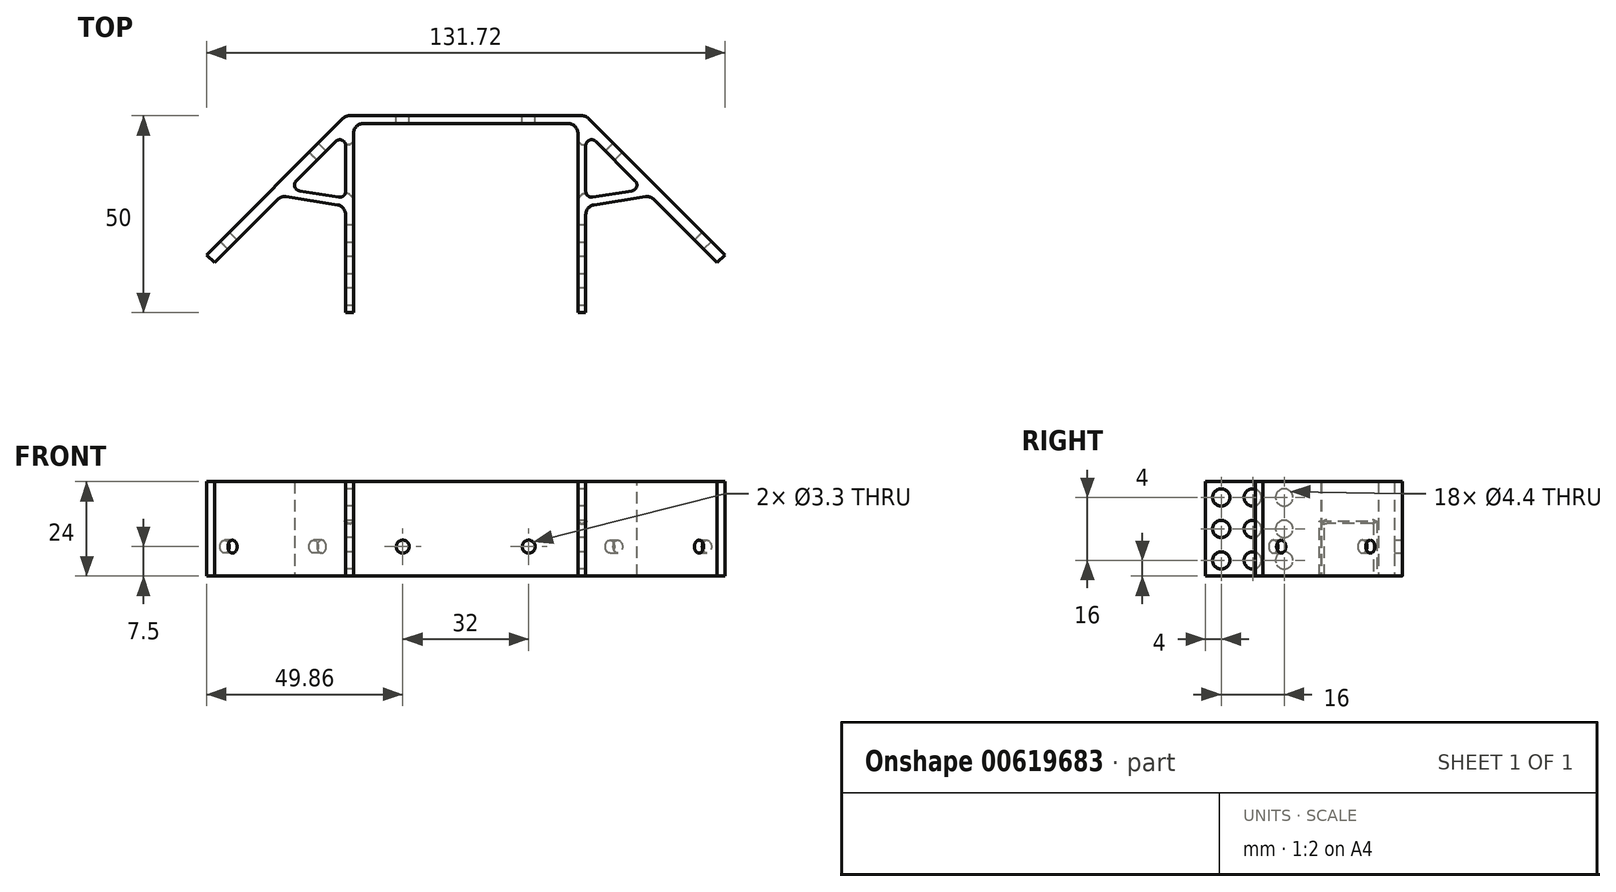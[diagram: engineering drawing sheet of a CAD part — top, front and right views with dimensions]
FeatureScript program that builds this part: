
annotation { "Feature Type Name" : "Feature", "Feature Type Description" : "" }
export const myFeature = defineFeature(function(context is Context, id is Id, definition is map)
    precondition{}
    {
        {
            var Q0;
            Q0=qCreatedBy(makeId("Top.planeOp"),FACE);
            var sketch = newSketch(context, id + "F0", { "sketchPlane" : qUnion([Q0])});
            skLineSegment(sketch, "E0.bottom", {"start": v(-28.5, 16) * mm, "end": v(28.5, 16) * mm});
            skLineSegment(sketch, "E0.left", {"start": v(-28.5, 16) * mm, "end": v(-28.5, -32) * mm});
            skLineSegment(sketch, "E0.right", {"start": v(28.5, 16) * mm, "end": v(28.5, -32) * mm});
            skLineSegment(sketch, "E1.bottom", {"start": v(-30.5, 18) * mm, "end": v(30.5, 18) * mm});
            skLineSegment(sketch, "E1.top", {"start": v(-30.5, -32) * mm, "end": v(-28.5, -32) * mm});
            skLineSegment(sketch, "E1.left", {"start": v(-30.5, 14) * mm, "end": v(-30.5, -2.97) * mm});
            skLineSegment(sketch, "E1.right", {"start": v(30.5, 14) * mm, "end": v(30.5, -2.97) * mm});
            skLineSegment(sketch, "E2", {"start": v(-30.5, 18) * mm, "end": v(-65.86, -17.36) * mm});
            skLineSegment(sketch, "E3", {"start": v(-30.5, 14) * mm, "end": v(-45.14, -0.64) * mm});
            skLineSegment(sketch, "E4", {"start": v(30.5, 18) * mm, "end": v(65.86, -17.36) * mm});
            skLineSegment(sketch, "E5", {"start": v(30.5, 14) * mm, "end": v(45.14, -0.64) * mm});
            skLineSegment(sketch, "E6", {"start": v(-65.86, -17.36) * mm, "end": v(-63.86, -19.36) * mm});
            skLineSegment(sketch, "E7", {"start": v(65.86, -17.36) * mm, "end": v(63.86, -19.36) * mm});
            skLineSegment(sketch, "E8.trimOffspring", {"start": v(28.5, -32) * mm, "end": v(30.5, -32) * mm});
            skLineSegment(sketch, "E9", {"start": v(-46.88, -2.38) * mm, "end": v(-30.5, -5) * mm});
            skLineSegment(sketch, "E10", {"start": v(-30.5, -2.97) * mm, "end": v(-45.14, -0.64) * mm});
            skLineSegment(sketch, "E11", {"start": v(30.5, -5) * mm, "end": v(46.88, -2.38) * mm});
            skLineSegment(sketch, "E12", {"start": v(45.14, -0.64) * mm, "end": v(30.5, -2.97) * mm});
            skLineSegment(sketch, "E13.trimOffspring", {"start": v(-46.88, -2.38) * mm, "end": v(-63.86, -19.36) * mm});
            skLineSegment(sketch, "E14.trimOffspring", {"start": v(-30.5, -5) * mm, "end": v(-30.5, -32) * mm});
            skLineSegment(sketch, "E15.trimOffspring", {"start": v(30.5, -5) * mm, "end": v(30.5, -32) * mm});
            skLineSegment(sketch, "E16.trimOffspring", {"start": v(46.88, -2.38) * mm, "end": v(63.86, -19.36) * mm});
            skSolve(sketch);
        }
        {
            var Q0;
            Q0=makeQuery(id+"F0.imprint","IMPRINT",FACE,{"disambiguationData":[TD([[makeQuery(id+"F0.imprint","IMPRINT",EDGE,{"derivedFrom":sQuery(id+"F0.wireOp",EDGE,"E0.bottom")}),1.0]])]});
            extrude(context, id + "F1", {"entities" : qUnion([Q0]), "depth" : 24 * mm, "offsetDistance" : 25 * mm});
        }
        {
            var Q0;
            Q0=makeQuery(id+"F1.opExtrude","SWEPT_FACE",FACE,{"disambiguationData":[OSD([sQuery(id+"F0.wireOp",EDGE,"E4")])]});
            var sketch = newSketch(context, id + "F2", { "sketchPlane" : qUnion([Q0])});
            skPoint(sketch, "E17", {"position": v(-20.34, 7.5) * mm});
            skPoint(sketch, "E18", {"position": v(-52.34, 7.5) * mm});
            skSolve(sketch);
        }
        {
            var Q0;
            Q0=sQuery(id+"F2.wireOp",VERTEX,"E17");
            var Q1;
            Q1=sQuery(id+"F2.wireOp",VERTEX,"E18");
            var Q2;
            Q2=makeQuery(id+"F1.opExtrude","SWEPT_BODY",BODY,{"disambiguationData":[OSD([sQuery(id+"F0.wireOp",EDGE,"E0.bottom"),sQuery(id+"F0.wireOp",EDGE,"E0.left"),sQuery(id+"F0.wireOp",EDGE,"E0.right"),sQuery(id+"F0.wireOp",EDGE,"E1.bottom"),sQuery(id+"F0.wireOp",EDGE,"E1.top"),sQuery(id+"F0.wireOp",EDGE,"E1.left"),sQuery(id+"F0.wireOp",EDGE,"E1.right"),sQuery(id+"F0.wireOp",EDGE,"E2"),sQuery(id+"F0.wireOp",EDGE,"E3"),sQuery(id+"F0.wireOp",EDGE,"E4"),sQuery(id+"F0.wireOp",EDGE,"E5"),sQuery(id+"F0.wireOp",EDGE,"E6"),sQuery(id+"F0.wireOp",EDGE,"E7"),sQuery(id+"F0.wireOp",EDGE,"E8.trimOffspring")])]});
            hole(context, id + "F3", {"style" : HoleStyle.SIMPLE, "endStyle" : HoleEndStyle.BLIND, "standardTappedOrClearance" : lookupTablePath({ "standard" : "ISO", "fit" : "Normal", "size" : "M3", "type" : "Clearance" }), "standardBlindInLast" : lookupTablePath({ "fit" : "Standard", "standard" : "ISO", "size" : "M3", "type" : "Clearance" }), "holeDiameter" : 3.3 * mm, "majorDiameter" : 3 * mm, "holeDepth" : 3 * mm, "isTappedThrough" : true, "tappedDepth" : 12 * mm, "tapClearance" : 3, "locations" : qUnion([Q0, Q1]), "scope" : qUnion([Q2])});
        }
        {
            var Q0;
            Q0=makeQuery(id+"F1.opExtrude","SWEPT_EDGE",EDGE,{"disambiguationData":[OSD([sQuery(id+"F0.wireOp",EDGE,"E1.left"),sQuery(id+"F0.wireOp",EDGE,"E3")])]});
            var Q1;
            Q1=makeQuery(id+"F1.opExtrude","SWEPT_EDGE",EDGE,{"disambiguationData":[OSD([sQuery(id+"F0.wireOp",EDGE,"E1.right"),sQuery(id+"F0.wireOp",EDGE,"E5")])]});
            var Q2;
            Q2=makeQuery(id+"F1.opExtrude","SWEPT_EDGE",EDGE,{"disambiguationData":[OSD([sQuery(id+"F0.wireOp",EDGE,"E3"),sQuery(id+"F0.wireOp",EDGE,"E10")])]});
            var Q3;
            Q3=makeQuery(id+"F1.opExtrude","SWEPT_EDGE",EDGE,{"disambiguationData":[OSD([sQuery(id+"F0.wireOp",EDGE,"E1.left"),sQuery(id+"F0.wireOp",EDGE,"E10")])]});
            var Q4;
            Q4=makeQuery(id+"F1.opExtrude","SWEPT_EDGE",EDGE,{"disambiguationData":[OSD([sQuery(id+"F0.wireOp",EDGE,"E1.right"),sQuery(id+"F0.wireOp",EDGE,"E12")])]});
            var Q5;
            Q5=makeQuery(id+"F1.opExtrude","SWEPT_EDGE",EDGE,{"disambiguationData":[OSD([sQuery(id+"F0.wireOp",EDGE,"E5"),sQuery(id+"F0.wireOp",EDGE,"E12")])]});
            fillet(context, id + "F4", {"entities" : qUnion([Q0, Q1, Q2, Q3, Q4, Q5]), "radius" : 1.5 * mm, "tangentPropagation" : true, "allowEdgeOverflow" : false});
        }
        {
            var Q0;
            Q0=makeQuery(id+"F1.opExtrude","SWEPT_FACE",FACE,{"disambiguationData":[OSD([sQuery(id+"F0.wireOp",EDGE,"E2")])]});
            var sketch = newSketch(context, id + "F5", { "sketchPlane" : qUnion([Q0])});
            skPoint(sketch, "E19", {"position": v(20.34, 7.5) * mm});
            skPoint(sketch, "E20", {"position": v(52.34, 7.5) * mm});
            skSolve(sketch);
        }
        {
            var Q0;
            Q0=sQuery(id+"F5.wireOp",VERTEX,"E19");
            var Q1;
            Q1=sQuery(id+"F5.wireOp",VERTEX,"E20");
            var Q2;
            Q2=makeQuery(id+"F1.opExtrude","SWEPT_BODY",BODY,{"disambiguationData":[OSD([sQuery(id+"F0.wireOp",EDGE,"E0.bottom"),sQuery(id+"F0.wireOp",EDGE,"E0.left"),sQuery(id+"F0.wireOp",EDGE,"E0.right"),sQuery(id+"F0.wireOp",EDGE,"E1.bottom"),sQuery(id+"F0.wireOp",EDGE,"E1.top"),sQuery(id+"F0.wireOp",EDGE,"E1.left"),sQuery(id+"F0.wireOp",EDGE,"E1.right"),sQuery(id+"F0.wireOp",EDGE,"E2"),sQuery(id+"F0.wireOp",EDGE,"E3"),sQuery(id+"F0.wireOp",EDGE,"E4"),sQuery(id+"F0.wireOp",EDGE,"E5"),sQuery(id+"F0.wireOp",EDGE,"E6"),sQuery(id+"F0.wireOp",EDGE,"E7"),sQuery(id+"F0.wireOp",EDGE,"E8.trimOffspring")])]});
            hole(context, id + "F6", {"style" : HoleStyle.SIMPLE, "endStyle" : HoleEndStyle.BLIND, "standardTappedOrClearance" : lookupTablePath({ "standard" : "ISO", "fit" : "Normal", "size" : "M3", "type" : "Clearance" }), "standardBlindInLast" : lookupTablePath({ "fit" : "Standard", "standard" : "ISO", "size" : "M3", "type" : "Clearance" }), "holeDiameter" : 3.3 * mm, "majorDiameter" : 5 * mm, "holeDepth" : 3 * mm, "isTappedThrough" : true, "tappedDepth" : 12 * mm, "tapClearance" : 3, "locations" : qUnion([Q0, Q1]), "scope" : qUnion([Q2])});
        }
        {
            var Q0;
            Q0=makeQuery(id+"F1.opExtrude","SWEPT_FACE",FACE,{"disambiguationData":[OSD([sQuery(id+"F0.wireOp",EDGE,"E1.bottom")])]});
            var sketch = newSketch(context, id + "F7", { "sketchPlane" : qUnion([Q0])});
            skPoint(sketch, "E21", {"position": v(-16, 7.5) * mm});
            skPoint(sketch, "E22", {"position": v(16, 7.5) * mm});
            skSolve(sketch);
        }
        {
            var Q0;
            Q0=sQuery(id+"F7.wireOp",VERTEX,"E21");
            var Q1;
            Q1=sQuery(id+"F7.wireOp",VERTEX,"E22");
            var Q2;
            Q2=makeQuery(id+"F1.opExtrude","SWEPT_BODY",BODY,{"disambiguationData":[OSD([sQuery(id+"F0.wireOp",EDGE,"E0.bottom"),sQuery(id+"F0.wireOp",EDGE,"E0.left"),sQuery(id+"F0.wireOp",EDGE,"E0.right"),sQuery(id+"F0.wireOp",EDGE,"E1.bottom"),sQuery(id+"F0.wireOp",EDGE,"E1.top"),sQuery(id+"F0.wireOp",EDGE,"E1.left"),sQuery(id+"F0.wireOp",EDGE,"E1.right"),sQuery(id+"F0.wireOp",EDGE,"E2"),sQuery(id+"F0.wireOp",EDGE,"E3"),sQuery(id+"F0.wireOp",EDGE,"E4"),sQuery(id+"F0.wireOp",EDGE,"E5"),sQuery(id+"F0.wireOp",EDGE,"E6"),sQuery(id+"F0.wireOp",EDGE,"E7"),sQuery(id+"F0.wireOp",EDGE,"E8.trimOffspring")])]});
            hole(context, id + "F8", {"style" : HoleStyle.SIMPLE, "endStyle" : HoleEndStyle.BLIND, "standardTappedOrClearance" : lookupTablePath({ "standard" : "ISO", "fit" : "Normal", "size" : "M3", "type" : "Clearance" }), "standardBlindInLast" : lookupTablePath({ "fit" : "Standard", "standard" : "ISO", "size" : "M3", "type" : "Clearance" }), "holeDiameter" : 3.3 * mm, "majorDiameter" : 5 * mm, "holeDepth" : 3 * mm, "isTappedThrough" : true, "tappedDepth" : 12 * mm, "tapClearance" : 3, "locations" : qUnion([Q0, Q1]), "scope" : qUnion([Q2])});
        }
        {
            var Q0;
            Q0=makeQuery(id+"F1.opExtrude","SWEPT_FACE",FACE,{"disambiguationData":[OSD([sQuery(id+"F0.wireOp",EDGE,"E1.left")])]});
            var sketch = newSketch(context, id + "F9", { "sketchPlane" : qUnion([Q0])});
            skPoint(sketch, "E23", {"position": v(28, 20) * mm});
            skPoint(sketch, "E24", {"position": v(28, 4) * mm});
            skPoint(sketch, "E25", {"position": v(20, 20) * mm});
            skPoint(sketch, "E26", {"position": v(20, 4) * mm});
            skPoint(sketch, "E27", {"position": v(12, 4) * mm});
            skPoint(sketch, "E28", {"position": v(12, 20) * mm});
            skPoint(sketch, "E29", {"position": v(28, 12) * mm});
            skPoint(sketch, "E30", {"position": v(20, 12) * mm});
            skPoint(sketch, "E31", {"position": v(12, 12) * mm});
            skSolve(sketch);
        }
        {
            var Q0;
            Q0=sQuery(id+"F9.wireOp",VERTEX,"E23");
            var Q1;
            Q1=sQuery(id+"F9.wireOp",VERTEX,"E24");
            var Q2;
            Q2=sQuery(id+"F9.wireOp",VERTEX,"E26");
            var Q3;
            Q3=sQuery(id+"F9.wireOp",VERTEX,"E25");
            var Q4;
            Q4=sQuery(id+"F9.wireOp",VERTEX,"E28");
            var Q5;
            Q5=sQuery(id+"F9.wireOp",VERTEX,"E27");
            var Q6;
            Q6=sQuery(id+"F9.wireOp",VERTEX,"E29");
            var Q7;
            Q7=sQuery(id+"F9.wireOp",VERTEX,"E30");
            var Q8;
            Q8=sQuery(id+"F9.wireOp",VERTEX,"E31");
            var Q9;
            Q9=makeQuery(id+"F1.opExtrude","SWEPT_BODY",BODY,{"disambiguationData":[OSD([sQuery(id+"F0.wireOp",EDGE,"E0.bottom"),sQuery(id+"F0.wireOp",EDGE,"E0.left"),sQuery(id+"F0.wireOp",EDGE,"E0.right"),sQuery(id+"F0.wireOp",EDGE,"E1.bottom"),sQuery(id+"F0.wireOp",EDGE,"E1.top"),sQuery(id+"F0.wireOp",EDGE,"E1.left"),sQuery(id+"F0.wireOp",EDGE,"E1.right"),sQuery(id+"F0.wireOp",EDGE,"E2"),sQuery(id+"F0.wireOp",EDGE,"E3"),sQuery(id+"F0.wireOp",EDGE,"E4"),sQuery(id+"F0.wireOp",EDGE,"E5"),sQuery(id+"F0.wireOp",EDGE,"E6"),sQuery(id+"F0.wireOp",EDGE,"E7"),sQuery(id+"F0.wireOp",EDGE,"E8.trimOffspring")])]});
            hole(context, id + "F10", {"style" : HoleStyle.SIMPLE, "endStyle" : HoleEndStyle.BLIND, "standardTappedOrClearance" : lookupTablePath({ "standard" : "ISO", "fit" : "Normal", "size" : "M4", "type" : "Clearance" }), "standardBlindInLast" : lookupTablePath({ "fit" : "Standard", "standard" : "ISO", "size" : "M4", "type" : "Clearance" }), "holeDiameter" : 4.4 * mm, "majorDiameter" : 3 * mm, "holeDepth" : 63 * mm, "isTappedThrough" : true, "tappedDepth" : 12 * mm, "tapClearance" : 3, "locations" : qUnion([Q0, Q1, Q2, Q3, Q4, Q5, Q6, Q7, Q8]), "scope" : qUnion([Q9])});
        }
        {
            var Q0;
            Q0=makeQuery(id+"F1.opExtrude","SWEPT_EDGE",EDGE,{"disambiguationData":[OSD([sQuery(id+"F0.wireOp",EDGE,"E1.bottom"),sQuery(id+"F0.wireOp",EDGE,"E2")])]});
            var Q1;
            Q1=makeQuery(id+"F1.opExtrude","SWEPT_EDGE",EDGE,{"disambiguationData":[OSD([sQuery(id+"F0.wireOp",EDGE,"E1.bottom"),sQuery(id+"F0.wireOp",EDGE,"E4")])]});
            var Q2;
            Q2=makeQuery(id+"F1.opExtrude","SWEPT_EDGE",EDGE,{"disambiguationData":[OSD([sQuery(id+"F0.wireOp",EDGE,"E0.bottom"),sQuery(id+"F0.wireOp",EDGE,"E0.left")])]});
            var Q3;
            Q3=makeQuery(id+"F1.opExtrude","SWEPT_EDGE",EDGE,{"disambiguationData":[OSD([sQuery(id+"F0.wireOp",EDGE,"E0.bottom"),sQuery(id+"F0.wireOp",EDGE,"E0.right")])]});
            var Q4;
            Q4=makeQuery(id+"F1.opExtrude","SWEPT_EDGE",EDGE,{"disambiguationData":[OSD([sQuery(id+"F0.wireOp",EDGE,"E11"),sQuery(id+"F0.wireOp",EDGE,"E15.trimOffspring")])]});
            var Q5;
            Q5=makeQuery(id+"F1.opExtrude","SWEPT_EDGE",EDGE,{"disambiguationData":[OSD([sQuery(id+"F0.wireOp",EDGE,"E11"),sQuery(id+"F0.wireOp",EDGE,"E16.trimOffspring")])]});
            var Q6;
            Q6=makeQuery(id+"F1.opExtrude","SWEPT_EDGE",EDGE,{"disambiguationData":[OSD([sQuery(id+"F0.wireOp",EDGE,"E9"),sQuery(id+"F0.wireOp",EDGE,"E13.trimOffspring")])]});
            var Q7;
            Q7=makeQuery(id+"F1.opExtrude","SWEPT_EDGE",EDGE,{"disambiguationData":[OSD([sQuery(id+"F0.wireOp",EDGE,"E9"),sQuery(id+"F0.wireOp",EDGE,"E14.trimOffspring")])]});
            fillet(context, id + "F11", {"entities" : qUnion([Q0, Q1, Q2, Q3, Q4, Q5, Q6, Q7]), "radius" : 2.5 * mm, "tangentPropagation" : true, "allowEdgeOverflow" : false});
        }
        {
            var Q0;
            Q0=makeQuery(id+"F1.opExtrude","SWEPT_FACE",FACE,{"disambiguationData":[OSD([sQuery(id+"F0.wireOp",EDGE,"E0.left")])]});
            var sketch = newSketch(context, id + "F12", { "sketchPlane" : qUnion([Q0])});
            skLineSegment(sketch, "E32.bottom", {"start": v(9.5, 0) * mm, "end": v(-1, 0) * mm});
            skLineSegment(sketch, "E32.top", {"start": v(9.5, 12) * mm, "end": v(-1, 12) * mm});
            skLineSegment(sketch, "E32.left", {"start": v(9.5, 0) * mm, "end": v(9.5, 12) * mm});
            skLineSegment(sketch, "E32.right", {"start": v(-1, 0) * mm, "end": v(-1, 12) * mm});
            skSolve(sketch);
        }
        {
            var Q0;
            Q0=makeQuery(id+"F12.imprint","IMPRINT",FACE,{"disambiguationData":[TD([[makeQuery(id+"F12.imprint","IMPRINT",EDGE,{"derivedFrom":sQuery(id+"F12.wireOp",EDGE,"E32.bottom")}),-1.0]])]});
            var Q1;
            Q1=makeQuery(id+"F1.opExtrude","SWEPT_FACE",FACE,{"disambiguationData":[OSD([sQuery(id+"F0.wireOp",EDGE,"E1.left")])]});
            var Q2;
            Q2=makeQuery(id+"F1.opExtrude","SWEPT_FACE",FACE,{"disambiguationData":[OSD([sQuery(id+"F0.wireOp",EDGE,"E1.right")])]});
            extrude(context, id + "F13", {"entities" : qUnion([Q0]), "operationType" : NewBodyOperationType.REMOVE, "endBound" : BoundingType.UP_TO_SURFACE, "oppositeDirection" : true, "depth" : 2.5 * mm, "endBoundEntityFace" : qUnion([Q1]), "offsetDistance" : 25 * mm, "hasSecondDirection" : true, "secondDirectionBound" : SecondDirectionBoundingType.UP_TO_SURFACE, "secondDirectionOppositeDirection" : false, "secondDirectionDepth" : 25 * mm, "secondDirectionBoundEntityFace" : qUnion([Q2])});
        }
        {
            var Q0;
            Q0=makeQuery(id+"F13.boolean.opBoolean","INTERSECT",EDGE,{"derivedFrom":[makeQuery(id+"F1.opExtrude","SWEPT_FACE",FACE,{"disambiguationData":[OSD([sQuery(id+"F0.wireOp",EDGE,"E0.right")])]}),makeQuery(id+"F13.opExtrude","SWEPT_FACE",FACE,{"disambiguationData":[OSD([sQuery(id+"F12.wireOp",EDGE,"E32.top")])]})]});
            var Q1;
            Q1=makeQuery(id+"F13.boolean.opBoolean","INTERSECT",EDGE,{"derivedFrom":[makeQuery(id+"F1.opExtrude","SWEPT_FACE",FACE,{"disambiguationData":[OSD([sQuery(id+"F0.wireOp",EDGE,"E0.right")])]}),makeQuery(id+"F13.opExtrude","SWEPT_FACE",FACE,{"disambiguationData":[OSD([sQuery(id+"F12.wireOp",EDGE,"E32.right")])]})]});
            var Q2;
            Q2=makeQuery(id+"F13.boolean.opBoolean","INTERSECT",EDGE,{"derivedFrom":[makeQuery(id+"F1.opExtrude","SWEPT_FACE",FACE,{"disambiguationData":[OSD([sQuery(id+"F0.wireOp",EDGE,"E0.right")])]}),makeQuery(id+"F13.opExtrude","SWEPT_FACE",FACE,{"disambiguationData":[OSD([sQuery(id+"F12.wireOp",EDGE,"E32.left")])]})]});
            var Q3;
            Q3=makeQuery(id+"F13.boolean.opBoolean","INTERSECT",EDGE,{"derivedFrom":[makeQuery(id+"F1.opExtrude","SWEPT_FACE",FACE,{"disambiguationData":[OSD([sQuery(id+"F0.wireOp",EDGE,"E0.left")])]}),makeQuery(id+"F13.opExtrude","SWEPT_FACE",FACE,{"disambiguationData":[OSD([sQuery(id+"F12.wireOp",EDGE,"E32.right")])]})]});
            var Q4;
            Q4=makeQuery(id+"F13.boolean.opBoolean","INTERSECT",EDGE,{"derivedFrom":[makeQuery(id+"F1.opExtrude","SWEPT_FACE",FACE,{"disambiguationData":[OSD([sQuery(id+"F0.wireOp",EDGE,"E0.left")])]}),makeQuery(id+"F13.opExtrude","SWEPT_FACE",FACE,{"disambiguationData":[OSD([sQuery(id+"F12.wireOp",EDGE,"E32.top")])]})]});
            var Q5;
            Q5=makeQuery(id+"F13.boolean.opBoolean","INTERSECT",EDGE,{"derivedFrom":[makeQuery(id+"F1.opExtrude","SWEPT_FACE",FACE,{"disambiguationData":[OSD([sQuery(id+"F0.wireOp",EDGE,"E0.left")])]}),makeQuery(id+"F13.opExtrude","SWEPT_FACE",FACE,{"disambiguationData":[OSD([sQuery(id+"F12.wireOp",EDGE,"E32.left")])]})]});
            chamfer(context, id + "F14", {"entities" : qUnion([Q0, Q1, Q2, Q3, Q4, Q5]), "width" : 2 * mm, "tangentPropagation" : true});
        }
        {
            var Q0;
            Q0=makeQuery(id+"F14.opChamfer","BLEND_EDGE",EDGE,{"blendedFrom":[makeQuery(id+"F13.boolean.opBoolean","INTERSECT",EDGE,{"derivedFrom":[makeQuery(id+"F1.opExtrude","SWEPT_FACE",FACE,{"disambiguationData":[OSD([sQuery(id+"F0.wireOp",EDGE,"E0.right")])]}),makeQuery(id+"F13.opExtrude","SWEPT_FACE",FACE,{"disambiguationData":[OSD([sQuery(id+"F12.wireOp",EDGE,"E32.top")])]})]}),makeQuery(id+"F1.opExtrude","SWEPT_FACE",FACE,{"disambiguationData":[OSD([sQuery(id+"F0.wireOp",EDGE,"E1.right")])]})],"blendedInto":[makeQuery(id+"F1.opExtrude","SWEPT_FACE",FACE,{"disambiguationData":[OSD([sQuery(id+"F0.wireOp",EDGE,"E1.right")])]})]});
            var Q1;
            Q1=makeQuery(id+"F14.opChamfer","BLEND_EDGE",EDGE,{"blendedFrom":[makeQuery(id+"F13.boolean.opBoolean","INTERSECT",EDGE,{"derivedFrom":[makeQuery(id+"F1.opExtrude","SWEPT_FACE",FACE,{"disambiguationData":[OSD([sQuery(id+"F0.wireOp",EDGE,"E0.left")])]}),makeQuery(id+"F13.opExtrude","SWEPT_FACE",FACE,{"disambiguationData":[OSD([sQuery(id+"F12.wireOp",EDGE,"E32.top")])]})]}),makeQuery(id+"F1.opExtrude","SWEPT_FACE",FACE,{"disambiguationData":[OSD([sQuery(id+"F0.wireOp",EDGE,"E1.left")])]})],"blendedInto":[makeQuery(id+"F1.opExtrude","SWEPT_FACE",FACE,{"disambiguationData":[OSD([sQuery(id+"F0.wireOp",EDGE,"E1.left")])]})]});
            var Q2;
            Q2=makeQuery(id+"F14.opChamfer","BLEND_EDGE",EDGE,{"blendedFrom":[makeQuery(id+"F13.boolean.opBoolean","INTERSECT",EDGE,{"derivedFrom":[makeQuery(id+"F1.opExtrude","SWEPT_FACE",FACE,{"disambiguationData":[OSD([sQuery(id+"F0.wireOp",EDGE,"E0.right")])]}),makeQuery(id+"F13.opExtrude","SWEPT_FACE",FACE,{"disambiguationData":[OSD([sQuery(id+"F12.wireOp",EDGE,"E32.right")])]})]}),makeQuery(id+"F1.opExtrude","SWEPT_FACE",FACE,{"disambiguationData":[OSD([sQuery(id+"F0.wireOp",EDGE,"E1.right")])]})],"blendedInto":[makeQuery(id+"F1.opExtrude","SWEPT_FACE",FACE,{"disambiguationData":[OSD([sQuery(id+"F0.wireOp",EDGE,"E1.right")])]})]});
            var Q3;
            Q3=makeQuery(id+"F14.opChamfer","BLEND_EDGE",EDGE,{"blendedFrom":[makeQuery(id+"F13.boolean.opBoolean","INTERSECT",EDGE,{"derivedFrom":[makeQuery(id+"F1.opExtrude","SWEPT_FACE",FACE,{"disambiguationData":[OSD([sQuery(id+"F0.wireOp",EDGE,"E0.right")])]}),makeQuery(id+"F13.opExtrude","SWEPT_FACE",FACE,{"disambiguationData":[OSD([sQuery(id+"F12.wireOp",EDGE,"E32.left")])]})]}),makeQuery(id+"F1.opExtrude","SWEPT_FACE",FACE,{"disambiguationData":[OSD([sQuery(id+"F0.wireOp",EDGE,"E1.right")])]})],"blendedInto":[makeQuery(id+"F1.opExtrude","SWEPT_FACE",FACE,{"disambiguationData":[OSD([sQuery(id+"F0.wireOp",EDGE,"E1.right")])]})]});
            var Q4;
            Q4=makeQuery(id+"F14.opChamfer","BLEND_EDGE",EDGE,{"blendedFrom":[makeQuery(id+"F13.boolean.opBoolean","INTERSECT",EDGE,{"derivedFrom":[makeQuery(id+"F1.opExtrude","SWEPT_FACE",FACE,{"disambiguationData":[OSD([sQuery(id+"F0.wireOp",EDGE,"E0.left")])]}),makeQuery(id+"F13.opExtrude","SWEPT_FACE",FACE,{"disambiguationData":[OSD([sQuery(id+"F12.wireOp",EDGE,"E32.right")])]})]}),makeQuery(id+"F1.opExtrude","SWEPT_FACE",FACE,{"disambiguationData":[OSD([sQuery(id+"F0.wireOp",EDGE,"E1.left")])]})],"blendedInto":[makeQuery(id+"F1.opExtrude","SWEPT_FACE",FACE,{"disambiguationData":[OSD([sQuery(id+"F0.wireOp",EDGE,"E1.left")])]})]});
            var Q5;
            Q5=makeQuery(id+"F14.opChamfer","BLEND_EDGE",EDGE,{"blendedFrom":[makeQuery(id+"F13.boolean.opBoolean","INTERSECT",EDGE,{"derivedFrom":[makeQuery(id+"F1.opExtrude","SWEPT_FACE",FACE,{"disambiguationData":[OSD([sQuery(id+"F0.wireOp",EDGE,"E0.left")])]}),makeQuery(id+"F13.opExtrude","SWEPT_FACE",FACE,{"disambiguationData":[OSD([sQuery(id+"F12.wireOp",EDGE,"E32.left")])]})]}),makeQuery(id+"F1.opExtrude","SWEPT_FACE",FACE,{"disambiguationData":[OSD([sQuery(id+"F0.wireOp",EDGE,"E1.left")])]})],"blendedInto":[makeQuery(id+"F1.opExtrude","SWEPT_FACE",FACE,{"disambiguationData":[OSD([sQuery(id+"F0.wireOp",EDGE,"E1.left")])]})]});
            fillet(context, id + "F15", {"entities" : qUnion([Q0, Q1, Q2, Q3, Q4, Q5]), "radius" : 1 * mm, "tangentPropagation" : true, "allowEdgeOverflow" : false});
        }
    });
